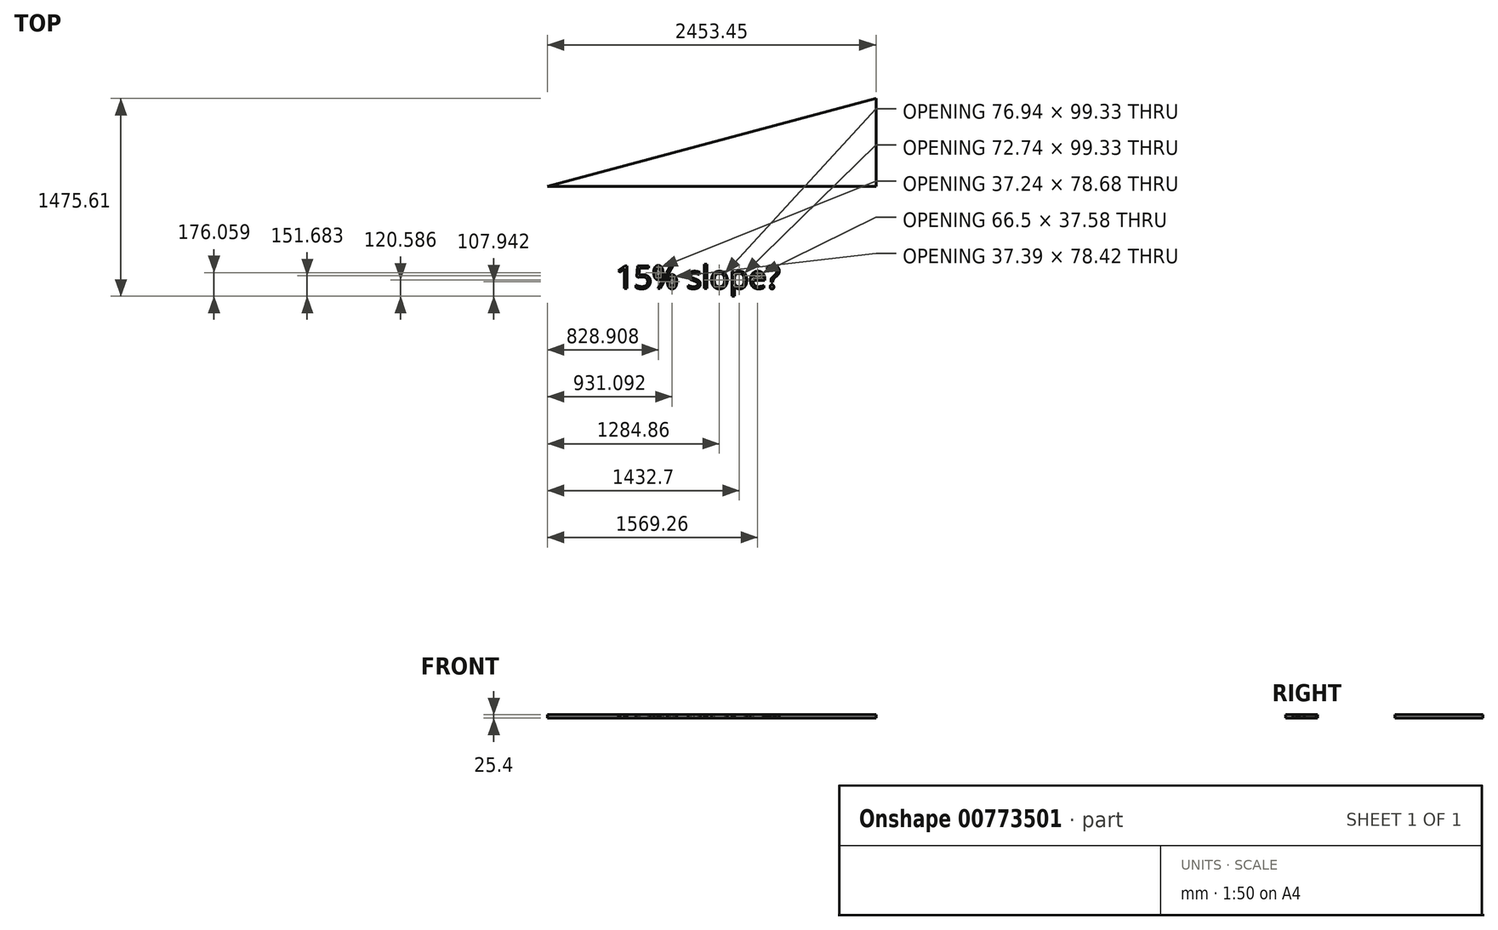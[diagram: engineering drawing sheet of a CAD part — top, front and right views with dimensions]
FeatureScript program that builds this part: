
annotation { "Feature Type Name" : "Feature", "Feature Type Description" : "" }
export const myFeature = defineFeature(function(context is Context, id is Id, definition is map)
    precondition{}
    {
        {
            var Q0;
            Q0=qCreatedBy(makeId("Top.planeOp"),FACE);
            var sketch = newSketch(context, id + "F0", { "sketchPlane" : qUnion([Q0])});
            skLineSegment(sketch, "E0", {"start": v(-1019.3, 0) * mm, "end": v(1434.15, 0) * mm});
            skLineSegment(sketch, "E1", {"start": v(1434.15, 0) * mm, "end": v(1434.15, 657.4) * mm});
            skLineSegment(sketch, "E2", {"start": v(1434.15, 657.4) * mm, "end": v(-1019.3, 0) * mm});
            skText(sketch, "E3", { "text": "15% slope?", "fontName": "OpenSans-Regular.ttf"});
            const initialGuessF0  = {"E3": [-0.50881, -0.7611, 1, 0, 0.1711]};
            skSetInitialGuess(sketch, initialGuessF0);
            skSolve(sketch);
        }
        {
            var Q0;
            Q0 = qSketchRegion(id + "F0", true);
            extrude(context, id + "F1", {"entities" : qUnion([Q0]), "depth" : 25.4 * mm, "offsetDistance" : 25.4 * mm});
        }
    });
